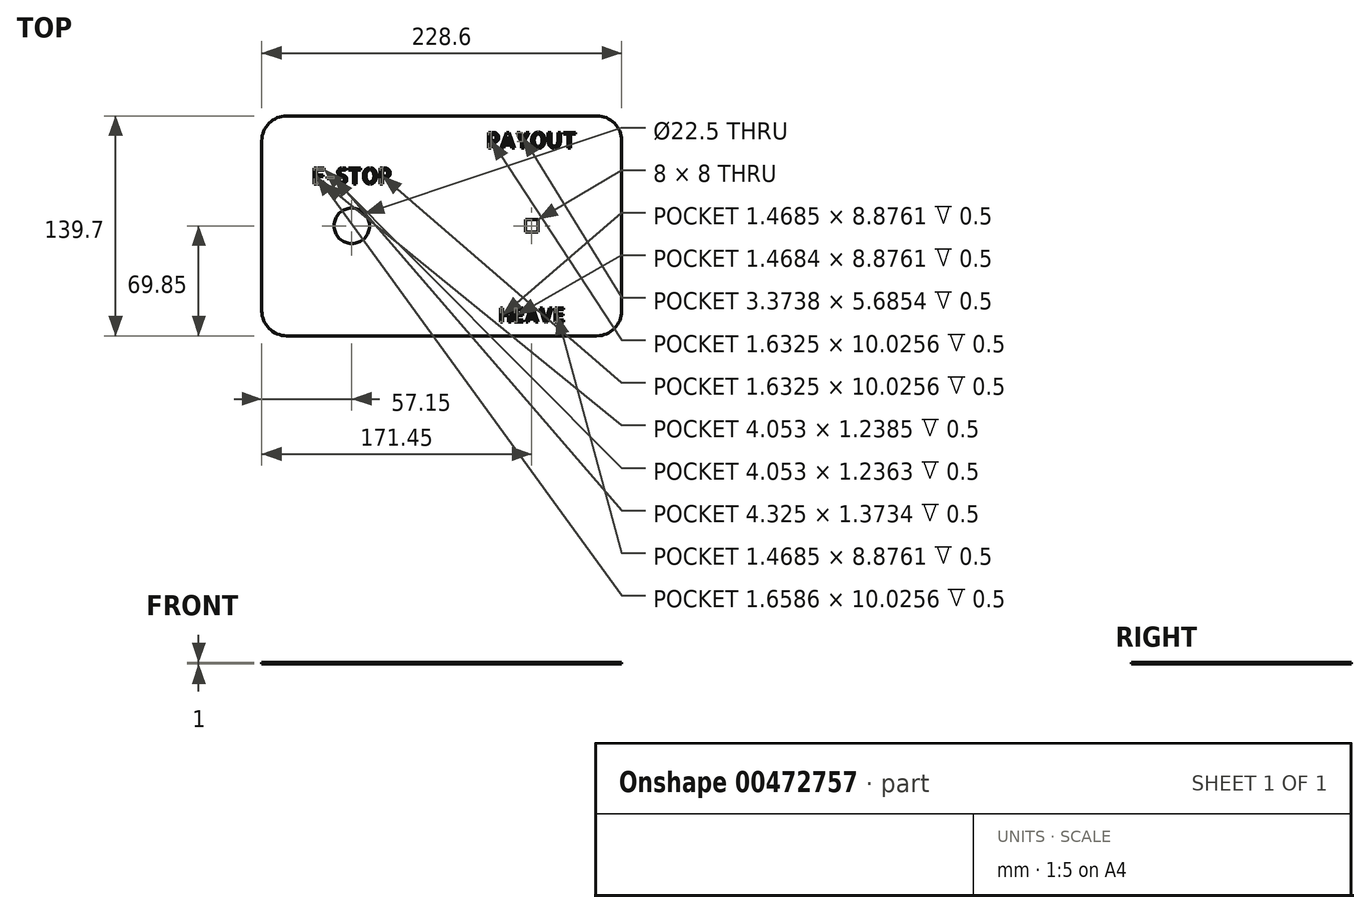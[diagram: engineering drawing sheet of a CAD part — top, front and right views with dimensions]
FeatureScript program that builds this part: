
annotation { "Feature Type Name" : "Feature", "Feature Type Description" : "" }
export const myFeature = defineFeature(function(context is Context, id is Id, definition is map)
    precondition{}
    {
        {
            var Q0;
            Q0=qCreatedBy(makeId("Top.planeOp"),FACE);
            var sketch = newSketch(context, id + "F0", { "sketchPlane" : qUnion([Q0])});
            skLineSegment(sketch, "E0.bottom", {"start": v(0, 0) * mm, "end": v(228.6, 0) * mm});
            skLineSegment(sketch, "E0.top", {"start": v(0, 139.7) * mm, "end": v(228.6, 139.7) * mm});
            skLineSegment(sketch, "E0.left", {"start": v(0, 0) * mm, "end": v(0, 139.7) * mm});
            skLineSegment(sketch, "E0.right", {"start": v(228.6, 0) * mm, "end": v(228.6, 139.7) * mm});
            skCircle(sketch, "E1", {"center": v(57.15, 69.85) * mm, "radius": 11.25 * mm});
            skLineSegment(sketch, "E2.bottom", {"start": v(167.45, 73.85) * mm, "end": v(175.45, 73.85) * mm});
            skLineSegment(sketch, "E2.top", {"start": v(167.45, 65.85) * mm, "end": v(175.45, 65.85) * mm});
            skLineSegment(sketch, "E2.left", {"start": v(167.45, 73.85) * mm, "end": v(167.45, 65.85) * mm});
            skLineSegment(sketch, "E2.right", {"start": v(175.45, 73.85) * mm, "end": v(175.45, 65.85) * mm});
            skSolve(sketch);
        }
        {
            var Q0;
            Q0 = qSketchRegion(id + "F0", true);
            extrude(context, id + "F1", {"entities" : qUnion([Q0]), "depth" : 1 * mm});
        }
        {
            var Q0;
            Q0=makeQuery(id+"F1.opExtrude","CAP_FACE",FACE,{"disambiguationData":[OSD([sQuery(id+"F0.wireOp",EDGE,"E0.bottom"),sQuery(id+"F0.wireOp",EDGE,"E0.top"),sQuery(id+"F0.wireOp",EDGE,"E0.left"),sQuery(id+"F0.wireOp",EDGE,"E0.right"),sQuery(id+"F0.wireOp",EDGE,"w9znDgtN-jEwp-FI1R-DwlJ-gQunYhQy7wCP.bottom"),sQuery(id+"F0.wireOp",EDGE,"w9znDgtN-jEwp-FI1R-DwlJ-gQunYhQy7wCP.top"),sQuery(id+"F0.wireOp",EDGE,"w9znDgtN-jEwp-FI1R-DwlJ-gQunYhQy7wCP.left"),sQuery(id+"F0.wireOp",EDGE,"w9znDgtN-jEwp-FI1R-DwlJ-gQunYhQy7wCP.right"),sQuery(id+"F0.wireOp",EDGE,"E1"),sQuery(id+"F0.wireOp",EDGE,"b33ce2e9-3de7-44f7-a6c2-fb7de444999e.sketch_text.stroke-0"),sQuery(id+"F0.wireOp",EDGE,"b33ce2e9-3de7-44f7-a6c2-fb7de444999e.sketch_text.stroke-1"),sQuery(id+"F0.wireOp",EDGE,"b33ce2e9-3de7-44f7-a6c2-fb7de444999e.sketch_text.stroke-2"),sQuery(id+"F0.wireOp",EDGE,"b33ce2e9-3de7-44f7-a6c2-fb7de444999e.sketch_text.stroke-3"),sQuery(id+"F0.wireOp",EDGE,"b33ce2e9-3de7-44f7-a6c2-fb7de444999e.sketch_text.stroke-4"),sQuery(id+"F0.wireOp",EDGE,"b33ce2e9-3de7-44f7-a6c2-fb7de444999e.sketch_text.stroke-5"),sQuery(id+"F0.wireOp",EDGE,"b33ce2e9-3de7-44f7-a6c2-fb7de444999e.sketch_text.stroke-6"),sQuery(id+"F0.wireOp",EDGE,"b33ce2e9-3de7-44f7-a6c2-fb7de444999e.sketch_text.stroke-7"),sQuery(id+"F0.wireOp",EDGE,"b33ce2e9-3de7-44f7-a6c2-fb7de444999e.sketch_text.stroke-8"),sQuery(id+"F0.wireOp",EDGE,"b33ce2e9-3de7-44f7-a6c2-fb7de444999e.sketch_text.stroke-9"),sQuery(id+"F0.wireOp",EDGE,"b33ce2e9-3de7-44f7-a6c2-fb7de444999e.sketch_text.stroke-10"),sQuery(id+"F0.wireOp",EDGE,"b33ce2e9-3de7-44f7-a6c2-fb7de444999e.sketch_text.stroke-11"),sQuery(id+"F0.wireOp",EDGE,"b33ce2e9-3de7-44f7-a6c2-fb7de444999e.sketch_text.stroke-12"),sQuery(id+"F0.wireOp",EDGE,"b33ce2e9-3de7-44f7-a6c2-fb7de444999e.sketch_text.stroke-13"),sQuery(id+"F0.wireOp",EDGE,"b33ce2e9-3de7-44f7-a6c2-fb7de444999e.sketch_text.stroke-14"),sQuery(id+"F0.wireOp",EDGE,"b33ce2e9-3de7-44f7-a6c2-fb7de444999e.sketch_text.stroke-15"),sQuery(id+"F0.wireOp",EDGE,"b33ce2e9-3de7-44f7-a6c2-fb7de444999e.sketch_text.stroke-16"),sQuery(id+"F0.wireOp",EDGE,"b33ce2e9-3de7-44f7-a6c2-fb7de444999e.sketch_text.stroke-17"),sQuery(id+"F0.wireOp",EDGE,"b33ce2e9-3de7-44f7-a6c2-fb7de444999e.sketch_text.stroke-18"),sQuery(id+"F0.wireOp",EDGE,"b33ce2e9-3de7-44f7-a6c2-fb7de444999e.sketch_text.stroke-19"),sQuery(id+"F0.wireOp",EDGE,"b33ce2e9-3de7-44f7-a6c2-fb7de444999e.sketch_text.stroke-20"),sQuery(id+"F0.wireOp",EDGE,"b33ce2e9-3de7-44f7-a6c2-fb7de444999e.sketch_text.stroke-21"),sQuery(id+"F0.wireOp",EDGE,"b33ce2e9-3de7-44f7-a6c2-fb7de444999e.sketch_text.stroke-22"),sQuery(id+"F0.wireOp",EDGE,"b33ce2e9-3de7-44f7-a6c2-fb7de444999e.sketch_text.stroke-23"),sQuery(id+"F0.wireOp",EDGE,"b33ce2e9-3de7-44f7-a6c2-fb7de444999e.sketch_text.stroke-24"),sQuery(id+"F0.wireOp",EDGE,"b33ce2e9-3de7-44f7-a6c2-fb7de444999e.sketch_text.stroke-25"),sQuery(id+"F0.wireOp",EDGE,"b33ce2e9-3de7-44f7-a6c2-fb7de444999e.sketch_text.stroke-26"),sQuery(id+"F0.wireOp",EDGE,"b33ce2e9-3de7-44f7-a6c2-fb7de444999e.sketch_text.stroke-27"),sQuery(id+"F0.wireOp",EDGE,"b33ce2e9-3de7-44f7-a6c2-fb7de444999e.sketch_text.stroke-28"),sQuery(id+"F0.wireOp",EDGE,"b33ce2e9-3de7-44f7-a6c2-fb7de444999e.sketch_text.stroke-29"),sQuery(id+"F0.wireOp",EDGE,"b33ce2e9-3de7-44f7-a6c2-fb7de444999e.sketch_text.stroke-30"),sQuery(id+"F0.wireOp",EDGE,"b33ce2e9-3de7-44f7-a6c2-fb7de444999e.sketch_text.stroke-31"),sQuery(id+"F0.wireOp",EDGE,"b33ce2e9-3de7-44f7-a6c2-fb7de444999e.sketch_text.stroke-32"),sQuery(id+"F0.wireOp",EDGE,"b33ce2e9-3de7-44f7-a6c2-fb7de444999e.sketch_text.stroke-33"),sQuery(id+"F0.wireOp",EDGE,"b33ce2e9-3de7-44f7-a6c2-fb7de444999e.sketch_text.stroke-34"),sQuery(id+"F0.wireOp",EDGE,"b33ce2e9-3de7-44f7-a6c2-fb7de444999e.sketch_text.stroke-35"),sQuery(id+"F0.wireOp",EDGE,"b33ce2e9-3de7-44f7-a6c2-fb7de444999e.sketch_text.stroke-36"),sQuery(id+"F0.wireOp",EDGE,"b33ce2e9-3de7-44f7-a6c2-fb7de444999e.sketch_text.stroke-37"),sQuery(id+"F0.wireOp",EDGE,"b33ce2e9-3de7-44f7-a6c2-fb7de444999e.sketch_text.stroke-38"),sQuery(id+"F0.wireOp",EDGE,"b33ce2e9-3de7-44f7-a6c2-fb7de444999e.sketch_text.stroke-39"),sQuery(id+"F0.wireOp",EDGE,"b33ce2e9-3de7-44f7-a6c2-fb7de444999e.sketch_text.stroke-40"),sQuery(id+"F0.wireOp",EDGE,"b33ce2e9-3de7-44f7-a6c2-fb7de444999e.sketch_text.stroke-41"),sQuery(id+"F0.wireOp",EDGE,"b33ce2e9-3de7-44f7-a6c2-fb7de444999e.sketch_text.stroke-42"),sQuery(id+"F0.wireOp",EDGE,"b33ce2e9-3de7-44f7-a6c2-fb7de444999e.sketch_text.stroke-43"),sQuery(id+"F0.wireOp",EDGE,"b33ce2e9-3de7-44f7-a6c2-fb7de444999e.sketch_text.stroke-44"),sQuery(id+"F0.wireOp",EDGE,"b33ce2e9-3de7-44f7-a6c2-fb7de444999e.sketch_text.stroke-45"),sQuery(id+"F0.wireOp",EDGE,"b33ce2e9-3de7-44f7-a6c2-fb7de444999e.sketch_text.stroke-46"),sQuery(id+"F0.wireOp",EDGE,"b33ce2e9-3de7-44f7-a6c2-fb7de444999e.sketch_text.stroke-47"),sQuery(id+"F0.wireOp",EDGE,"b33ce2e9-3de7-44f7-a6c2-fb7de444999e.sketch_text.stroke-48"),sQuery(id+"F0.wireOp",EDGE,"b33ce2e9-3de7-44f7-a6c2-fb7de444999e.sketch_text.stroke-49"),sQuery(id+"F0.wireOp",EDGE,"b33ce2e9-3de7-44f7-a6c2-fb7de444999e.sketch_text.stroke-50"),sQuery(id+"F0.wireOp",EDGE,"b33ce2e9-3de7-44f7-a6c2-fb7de444999e.sketch_text.stroke-51"),sQuery(id+"F0.wireOp",EDGE,"b33ce2e9-3de7-44f7-a6c2-fb7de444999e.sketch_text.stroke-52"),sQuery(id+"F0.wireOp",EDGE,"b33ce2e9-3de7-44f7-a6c2-fb7de444999e.sketch_text.stroke-53"),sQuery(id+"F0.wireOp",EDGE,"b33ce2e9-3de7-44f7-a6c2-fb7de444999e.sketch_text.stroke-54"),sQuery(id+"F0.wireOp",EDGE,"b33ce2e9-3de7-44f7-a6c2-fb7de444999e.sketch_text.stroke-55"),sQuery(id+"F0.wireOp",EDGE,"b33ce2e9-3de7-44f7-a6c2-fb7de444999e.sketch_text.stroke-56"),sQuery(id+"F0.wireOp",EDGE,"b33ce2e9-3de7-44f7-a6c2-fb7de444999e.sketch_text.stroke-57"),sQuery(id+"F0.wireOp",EDGE,"b33ce2e9-3de7-44f7-a6c2-fb7de444999e.sketch_text.stroke-58"),sQuery(id+"F0.wireOp",EDGE,"b33ce2e9-3de7-44f7-a6c2-fb7de444999e.sketch_text.stroke-59"),sQuery(id+"F0.wireOp",EDGE,"b33ce2e9-3de7-44f7-a6c2-fb7de444999e.sketch_text.stroke-60"),sQuery(id+"F0.wireOp",EDGE,"b33ce2e9-3de7-44f7-a6c2-fb7de444999e.sketch_text.stroke-61"),sQuery(id+"F0.wireOp",EDGE,"b33ce2e9-3de7-44f7-a6c2-fb7de444999e.sketch_text.stroke-62"),sQuery(id+"F0.wireOp",EDGE,"b33ce2e9-3de7-44f7-a6c2-fb7de444999e.sketch_text.stroke-63"),sQuery(id+"F0.wireOp",EDGE,"b33ce2e9-3de7-44f7-a6c2-fb7de444999e.sketch_text.stroke-64"),sQuery(id+"F0.wireOp",EDGE,"b33ce2e9-3de7-44f7-a6c2-fb7de444999e.sketch_text.stroke-65"),sQuery(id+"F0.wireOp",EDGE,"b33ce2e9-3de7-44f7-a6c2-fb7de444999e.sketch_text.stroke-66"),sQuery(id+"F0.wireOp",EDGE,"b33ce2e9-3de7-44f7-a6c2-fb7de444999e.sketch_text.stroke-67"),sQuery(id+"F0.wireOp",EDGE,"b33ce2e9-3de7-44f7-a6c2-fb7de444999e.sketch_text.stroke-68"),sQuery(id+"F0.wireOp",EDGE,"b33ce2e9-3de7-44f7-a6c2-fb7de444999e.sketch_text.stroke-69"),sQuery(id+"F0.wireOp",EDGE,"b33ce2e9-3de7-44f7-a6c2-fb7de444999e.sketch_text.stroke-70"),sQuery(id+"F0.wireOp",EDGE,"b33ce2e9-3de7-44f7-a6c2-fb7de444999e.sketch_text.stroke-71"),sQuery(id+"F0.wireOp",EDGE,"b33ce2e9-3de7-44f7-a6c2-fb7de444999e.sketch_text.stroke-72"),sQuery(id+"F0.wireOp",EDGE,"b33ce2e9-3de7-44f7-a6c2-fb7de444999e.sketch_text.stroke-73"),sQuery(id+"F0.wireOp",EDGE,"b33ce2e9-3de7-44f7-a6c2-fb7de444999e.sketch_text.stroke-74"),sQuery(id+"F0.wireOp",EDGE,"b33ce2e9-3de7-44f7-a6c2-fb7de444999e.sketch_text.stroke-75"),sQuery(id+"F0.wireOp",EDGE,"b33ce2e9-3de7-44f7-a6c2-fb7de444999e.sketch_text.stroke-76"),sQuery(id+"F0.wireOp",EDGE,"b33ce2e9-3de7-44f7-a6c2-fb7de444999e.sketch_text.stroke-77"),sQuery(id+"F0.wireOp",EDGE,"b33ce2e9-3de7-44f7-a6c2-fb7de444999e.sketch_text.stroke-78"),sQuery(id+"F0.wireOp",EDGE,"b33ce2e9-3de7-44f7-a6c2-fb7de444999e.sketch_text.stroke-79"),sQuery(id+"F0.wireOp",EDGE,"b33ce2e9-3de7-44f7-a6c2-fb7de444999e.sketch_text.stroke-80"),sQuery(id+"F0.wireOp",EDGE,"b33ce2e9-3de7-44f7-a6c2-fb7de444999e.sketch_text.stroke-81"),sQuery(id+"F0.wireOp",EDGE,"b33ce2e9-3de7-44f7-a6c2-fb7de444999e.sketch_text.stroke-82"),sQuery(id+"F0.wireOp",EDGE,"b33ce2e9-3de7-44f7-a6c2-fb7de444999e.sketch_text.stroke-83"),sQuery(id+"F0.wireOp",EDGE,"b33ce2e9-3de7-44f7-a6c2-fb7de444999e.sketch_text.stroke-84"),sQuery(id+"F0.wireOp",EDGE,"b33ce2e9-3de7-44f7-a6c2-fb7de444999e.sketch_text.stroke-85"),sQuery(id+"F0.wireOp",EDGE,"b33ce2e9-3de7-44f7-a6c2-fb7de444999e.sketch_text.stroke-86"),sQuery(id+"F0.wireOp",EDGE,"b33ce2e9-3de7-44f7-a6c2-fb7de444999e.sketch_text.stroke-87"),sQuery(id+"F0.wireOp",EDGE,"b33ce2e9-3de7-44f7-a6c2-fb7de444999e.sketch_text.stroke-88"),sQuery(id+"F0.wireOp",EDGE,"b33ce2e9-3de7-44f7-a6c2-fb7de444999e.sketch_text.stroke-89"),sQuery(id+"F0.wireOp",EDGE,"b33ce2e9-3de7-44f7-a6c2-fb7de444999e.sketch_text.stroke-90"),sQuery(id+"F0.wireOp",EDGE,"b33ce2e9-3de7-44f7-a6c2-fb7de444999e.sketch_text.stroke-91"),sQuery(id+"F0.wireOp",EDGE,"b33ce2e9-3de7-44f7-a6c2-fb7de444999e.sketch_text.stroke-92"),sQuery(id+"F0.wireOp",EDGE,"b33ce2e9-3de7-44f7-a6c2-fb7de444999e.sketch_text.stroke-93"),sQuery(id+"F0.wireOp",EDGE,"b33ce2e9-3de7-44f7-a6c2-fb7de444999e.sketch_text.stroke-94"),sQuery(id+"F0.wireOp",EDGE,"b33ce2e9-3de7-44f7-a6c2-fb7de444999e.sketch_text.stroke-95"),sQuery(id+"F0.wireOp",EDGE,"b33ce2e9-3de7-44f7-a6c2-fb7de444999e.sketch_text.stroke-96"),sQuery(id+"F0.wireOp",EDGE,"b33ce2e9-3de7-44f7-a6c2-fb7de444999e.sketch_text.stroke-97"),sQuery(id+"F0.wireOp",EDGE,"b33ce2e9-3de7-44f7-a6c2-fb7de444999e.sketch_text.stroke-98"),sQuery(id+"F0.wireOp",EDGE,"b33ce2e9-3de7-44f7-a6c2-fb7de444999e.sketch_text.stroke-99"),sQuery(id+"F0.wireOp",EDGE,"b33ce2e9-3de7-44f7-a6c2-fb7de444999e.sketch_text.stroke-100"),sQuery(id+"F0.wireOp",EDGE,"b33ce2e9-3de7-44f7-a6c2-fb7de444999e.sketch_text.stroke-101"),sQuery(id+"F0.wireOp",EDGE,"b33ce2e9-3de7-44f7-a6c2-fb7de444999e.sketch_text.stroke-102"),sQuery(id+"F0.wireOp",EDGE,"b33ce2e9-3de7-44f7-a6c2-fb7de444999e.sketch_text.stroke-103"),sQuery(id+"F0.wireOp",EDGE,"b33ce2e9-3de7-44f7-a6c2-fb7de444999e.sketch_text.stroke-104"),sQuery(id+"F0.wireOp",EDGE,"b33ce2e9-3de7-44f7-a6c2-fb7de444999e.sketch_text.stroke-105"),sQuery(id+"F0.wireOp",EDGE,"b33ce2e9-3de7-44f7-a6c2-fb7de444999e.sketch_text.stroke-106"),sQuery(id+"F0.wireOp",EDGE,"b33ce2e9-3de7-44f7-a6c2-fb7de444999e.sketch_text.stroke-107"),sQuery(id+"F0.wireOp",EDGE,"b33ce2e9-3de7-44f7-a6c2-fb7de444999e.sketch_text.stroke-108"),sQuery(id+"F0.wireOp",EDGE,"b33ce2e9-3de7-44f7-a6c2-fb7de444999e.sketch_text.stroke-109"),sQuery(id+"F0.wireOp",EDGE,"b33ce2e9-3de7-44f7-a6c2-fb7de444999e.sketch_text.stroke-110"),sQuery(id+"F0.wireOp",EDGE,"b33ce2e9-3de7-44f7-a6c2-fb7de444999e.sketch_text.stroke-111"),sQuery(id+"F0.wireOp",EDGE,"b33ce2e9-3de7-44f7-a6c2-fb7de444999e.sketch_text.stroke-112"),sQuery(id+"F0.wireOp",EDGE,"b33ce2e9-3de7-44f7-a6c2-fb7de444999e.sketch_text.stroke-113"),sQuery(id+"F0.wireOp",EDGE,"b33ce2e9-3de7-44f7-a6c2-fb7de444999e.sketch_text.stroke-114"),sQuery(id+"F0.wireOp",EDGE,"b33ce2e9-3de7-44f7-a6c2-fb7de444999e.sketch_text.stroke-115"),sQuery(id+"F0.wireOp",EDGE,"b33ce2e9-3de7-44f7-a6c2-fb7de444999e.sketch_text.stroke-116"),sQuery(id+"F0.wireOp",EDGE,"b33ce2e9-3de7-44f7-a6c2-fb7de444999e.sketch_text.stroke-117"),sQuery(id+"F0.wireOp",EDGE,"b33ce2e9-3de7-44f7-a6c2-fb7de444999e.sketch_text.stroke-118"),sQuery(id+"F0.wireOp",EDGE,"b33ce2e9-3de7-44f7-a6c2-fb7de444999e.sketch_text.stroke-119"),sQuery(id+"F0.wireOp",EDGE,"b33ce2e9-3de7-44f7-a6c2-fb7de444999e.sketch_text.stroke-120"),sQuery(id+"F0.wireOp",EDGE,"b33ce2e9-3de7-44f7-a6c2-fb7de444999e.sketch_text.stroke-121"),sQuery(id+"F0.wireOp",EDGE,"b33ce2e9-3de7-44f7-a6c2-fb7de444999e.sketch_text.stroke-122"),sQuery(id+"F0.wireOp",EDGE,"b33ce2e9-3de7-44f7-a6c2-fb7de444999e.sketch_text.stroke-123"),sQuery(id+"F0.wireOp",EDGE,"b33ce2e9-3de7-44f7-a6c2-fb7de444999e.sketch_text.stroke-124"),sQuery(id+"F0.wireOp",EDGE,"b33ce2e9-3de7-44f7-a6c2-fb7de444999e.sketch_text.stroke-125"),sQuery(id+"F0.wireOp",EDGE,"b33ce2e9-3de7-44f7-a6c2-fb7de444999e.sketch_text.stroke-126"),sQuery(id+"F0.wireOp",EDGE,"b33ce2e9-3de7-44f7-a6c2-fb7de444999e.sketch_text.stroke-127"),sQuery(id+"F0.wireOp",EDGE,"b33ce2e9-3de7-44f7-a6c2-fb7de444999e.sketch_text.stroke-128"),sQuery(id+"F0.wireOp",EDGE,"b33ce2e9-3de7-44f7-a6c2-fb7de444999e.sketch_text.stroke-129"),sQuery(id+"F0.wireOp",EDGE,"b33ce2e9-3de7-44f7-a6c2-fb7de444999e.sketch_text.stroke-130"),sQuery(id+"F0.wireOp",EDGE,"b33ce2e9-3de7-44f7-a6c2-fb7de444999e.sketch_text.stroke-131"),sQuery(id+"F0.wireOp",EDGE,"b33ce2e9-3de7-44f7-a6c2-fb7de444999e.sketch_text.stroke-132"),sQuery(id+"F0.wireOp",EDGE,"b33ce2e9-3de7-44f7-a6c2-fb7de444999e.sketch_text.stroke-133"),sQuery(id+"F0.wireOp",EDGE,"b33ce2e9-3de7-44f7-a6c2-fb7de444999e.sketch_text.stroke-134"),sQuery(id+"F0.wireOp",EDGE,"b33ce2e9-3de7-44f7-a6c2-fb7de444999e.sketch_text.stroke-135"),sQuery(id+"F0.wireOp",EDGE,"b33ce2e9-3de7-44f7-a6c2-fb7de444999e.sketch_text.stroke-136"),sQuery(id+"F0.wireOp",EDGE,"b33ce2e9-3de7-44f7-a6c2-fb7de444999e.sketch_text.stroke-137"),sQuery(id+"F0.wireOp",EDGE,"b33ce2e9-3de7-44f7-a6c2-fb7de444999e.sketch_text.stroke-138"),sQuery(id+"F0.wireOp",EDGE,"b33ce2e9-3de7-44f7-a6c2-fb7de444999e.sketch_text.stroke-139"),sQuery(id+"F0.wireOp",EDGE,"227bb859-5d3c-4ea1-9f34-01fb2c13be0c.sketch_text.stroke-0"),sQuery(id+"F0.wireOp",EDGE,"227bb859-5d3c-4ea1-9f34-01fb2c13be0c.sketch_text.stroke-1"),sQuery(id+"F0.wireOp",EDGE,"227bb859-5d3c-4ea1-9f34-01fb2c13be0c.sketch_text.stroke-2"),sQuery(id+"F0.wireOp",EDGE,"227bb859-5d3c-4ea1-9f34-01fb2c13be0c.sketch_text.stroke-3"),sQuery(id+"F0.wireOp",EDGE,"227bb859-5d3c-4ea1-9f34-01fb2c13be0c.sketch_text.stroke-4"),sQuery(id+"F0.wireOp",EDGE,"227bb859-5d3c-4ea1-9f34-01fb2c13be0c.sketch_text.stroke-5"),sQuery(id+"F0.wireOp",EDGE,"227bb859-5d3c-4ea1-9f34-01fb2c13be0c.sketch_text.stroke-6"),sQuery(id+"F0.wireOp",EDGE,"227bb859-5d3c-4ea1-9f34-01fb2c13be0c.sketch_text.stroke-7"),sQuery(id+"F0.wireOp",EDGE,"227bb859-5d3c-4ea1-9f34-01fb2c13be0c.sketch_text.stroke-8"),sQuery(id+"F0.wireOp",EDGE,"227bb859-5d3c-4ea1-9f34-01fb2c13be0c.sketch_text.stroke-9"),sQuery(id+"F0.wireOp",EDGE,"227bb859-5d3c-4ea1-9f34-01fb2c13be0c.sketch_text.stroke-10"),sQuery(id+"F0.wireOp",EDGE,"227bb859-5d3c-4ea1-9f34-01fb2c13be0c.sketch_text.stroke-11"),sQuery(id+"F0.wireOp",EDGE,"227bb859-5d3c-4ea1-9f34-01fb2c13be0c.sketch_text.stroke-12"),sQuery(id+"F0.wireOp",EDGE,"227bb859-5d3c-4ea1-9f34-01fb2c13be0c.sketch_text.stroke-13"),sQuery(id+"F0.wireOp",EDGE,"227bb859-5d3c-4ea1-9f34-01fb2c13be0c.sketch_text.stroke-14"),sQuery(id+"F0.wireOp",EDGE,"227bb859-5d3c-4ea1-9f34-01fb2c13be0c.sketch_text.stroke-15"),sQuery(id+"F0.wireOp",EDGE,"227bb859-5d3c-4ea1-9f34-01fb2c13be0c.sketch_text.stroke-16"),sQuery(id+"F0.wireOp",EDGE,"227bb859-5d3c-4ea1-9f34-01fb2c13be0c.sketch_text.stroke-17"),sQuery(id+"F0.wireOp",EDGE,"227bb859-5d3c-4ea1-9f34-01fb2c13be0c.sketch_text.stroke-18"),sQuery(id+"F0.wireOp",EDGE,"227bb859-5d3c-4ea1-9f34-01fb2c13be0c.sketch_text.stroke-19"),sQuery(id+"F0.wireOp",EDGE,"227bb859-5d3c-4ea1-9f34-01fb2c13be0c.sketch_text.stroke-20"),sQuery(id+"F0.wireOp",EDGE,"227bb859-5d3c-4ea1-9f34-01fb2c13be0c.sketch_text.stroke-21"),sQuery(id+"F0.wireOp",EDGE,"227bb859-5d3c-4ea1-9f34-01fb2c13be0c.sketch_text.stroke-22"),sQuery(id+"F0.wireOp",EDGE,"227bb859-5d3c-4ea1-9f34-01fb2c13be0c.sketch_text.stroke-23"),sQuery(id+"F0.wireOp",EDGE,"227bb859-5d3c-4ea1-9f34-01fb2c13be0c.sketch_text.stroke-24"),sQuery(id+"F0.wireOp",EDGE,"227bb859-5d3c-4ea1-9f34-01fb2c13be0c.sketch_text.stroke-25"),sQuery(id+"F0.wireOp",EDGE,"227bb859-5d3c-4ea1-9f34-01fb2c13be0c.sketch_text.stroke-26"),sQuery(id+"F0.wireOp",EDGE,"227bb859-5d3c-4ea1-9f34-01fb2c13be0c.sketch_text.stroke-27"),sQuery(id+"F0.wireOp",EDGE,"227bb859-5d3c-4ea1-9f34-01fb2c13be0c.sketch_text.stroke-28"),sQuery(id+"F0.wireOp",EDGE,"227bb859-5d3c-4ea1-9f34-01fb2c13be0c.sketch_text.stroke-29"),sQuery(id+"F0.wireOp",EDGE,"227bb859-5d3c-4ea1-9f34-01fb2c13be0c.sketch_text.stroke-30"),sQuery(id+"F0.wireOp",EDGE,"227bb859-5d3c-4ea1-9f34-01fb2c13be0c.sketch_text.stroke-31"),sQuery(id+"F0.wireOp",EDGE,"227bb859-5d3c-4ea1-9f34-01fb2c13be0c.sketch_text.stroke-32"),sQuery(id+"F0.wireOp",EDGE,"227bb859-5d3c-4ea1-9f34-01fb2c13be0c.sketch_text.stroke-33"),sQuery(id+"F0.wireOp",EDGE,"227bb859-5d3c-4ea1-9f34-01fb2c13be0c.sketch_text.stroke-34"),sQuery(id+"F0.wireOp",EDGE,"227bb859-5d3c-4ea1-9f34-01fb2c13be0c.sketch_text.stroke-35"),sQuery(id+"F0.wireOp",EDGE,"227bb859-5d3c-4ea1-9f34-01fb2c13be0c.sketch_text.stroke-36"),sQuery(id+"F0.wireOp",EDGE,"227bb859-5d3c-4ea1-9f34-01fb2c13be0c.sketch_text.stroke-37"),sQuery(id+"F0.wireOp",EDGE,"227bb859-5d3c-4ea1-9f34-01fb2c13be0c.sketch_text.stroke-38"),sQuery(id+"F0.wireOp",EDGE,"227bb859-5d3c-4ea1-9f34-01fb2c13be0c.sketch_text.stroke-39"),sQuery(id+"F0.wireOp",EDGE,"227bb859-5d3c-4ea1-9f34-01fb2c13be0c.sketch_text.stroke-40"),sQuery(id+"F0.wireOp",EDGE,"227bb859-5d3c-4ea1-9f34-01fb2c13be0c.sketch_text.stroke-41"),sQuery(id+"F0.wireOp",EDGE,"227bb859-5d3c-4ea1-9f34-01fb2c13be0c.sketch_text.stroke-42"),sQuery(id+"F0.wireOp",EDGE,"227bb859-5d3c-4ea1-9f34-01fb2c13be0c.sketch_text.stroke-43"),sQuery(id+"F0.wireOp",EDGE,"227bb859-5d3c-4ea1-9f34-01fb2c13be0c.sketch_text.stroke-44"),sQuery(id+"F0.wireOp",EDGE,"227bb859-5d3c-4ea1-9f34-01fb2c13be0c.sketch_text.stroke-45"),sQuery(id+"F0.wireOp",EDGE,"227bb859-5d3c-4ea1-9f34-01fb2c13be0c.sketch_text.stroke-46"),sQuery(id+"F0.wireOp",EDGE,"227bb859-5d3c-4ea1-9f34-01fb2c13be0c.sketch_text.stroke-47"),sQuery(id+"F0.wireOp",EDGE,"227bb859-5d3c-4ea1-9f34-01fb2c13be0c.sketch_text.stroke-48"),sQuery(id+"F0.wireOp",EDGE,"227bb859-5d3c-4ea1-9f34-01fb2c13be0c.sketch_text.stroke-49"),sQuery(id+"F0.wireOp",EDGE,"227bb859-5d3c-4ea1-9f34-01fb2c13be0c.sketch_text.stroke-50"),sQuery(id+"F0.wireOp",EDGE,"227bb859-5d3c-4ea1-9f34-01fb2c13be0c.sketch_text.stroke-51"),sQuery(id+"F0.wireOp",EDGE,"227bb859-5d3c-4ea1-9f34-01fb2c13be0c.sketch_text.stroke-52"),sQuery(id+"F0.wireOp",EDGE,"227bb859-5d3c-4ea1-9f34-01fb2c13be0c.sketch_text.stroke-53"),sQuery(id+"F0.wireOp",EDGE,"227bb859-5d3c-4ea1-9f34-01fb2c13be0c.sketch_text.stroke-54"),sQuery(id+"F0.wireOp",EDGE,"227bb859-5d3c-4ea1-9f34-01fb2c13be0c.sketch_text.stroke-55"),sQuery(id+"F0.wireOp",EDGE,"227bb859-5d3c-4ea1-9f34-01fb2c13be0c.sketch_text.stroke-56"),sQuery(id+"F0.wireOp",EDGE,"227bb859-5d3c-4ea1-9f34-01fb2c13be0c.sketch_text.stroke-57"),sQuery(id+"F0.wireOp",EDGE,"227bb859-5d3c-4ea1-9f34-01fb2c13be0c.sketch_text.stroke-58"),sQuery(id+"F0.wireOp",EDGE,"227bb859-5d3c-4ea1-9f34-01fb2c13be0c.sketch_text.stroke-59"),sQuery(id+"F0.wireOp",EDGE,"227bb859-5d3c-4ea1-9f34-01fb2c13be0c.sketch_text.stroke-60"),sQuery(id+"F0.wireOp",EDGE,"227bb859-5d3c-4ea1-9f34-01fb2c13be0c.sketch_text.stroke-61"),sQuery(id+"F0.wireOp",EDGE,"227bb859-5d3c-4ea1-9f34-01fb2c13be0c.sketch_text.stroke-62"),sQuery(id+"F0.wireOp",EDGE,"227bb859-5d3c-4ea1-9f34-01fb2c13be0c.sketch_text.stroke-63"),sQuery(id+"F0.wireOp",EDGE,"227bb859-5d3c-4ea1-9f34-01fb2c13be0c.sketch_text.stroke-64")])],"isStart":false});
            var sketch = newSketch(context, id + "F2", { "sketchPlane" : qUnion([Q0])});
            skText(sketch, "E3", { "text": "PAYOUT", "fontName": "AllertaStencil-Regular.ttf"});
            skText(sketch, "E4", { "text": "E-STOP", "fontName": "AllertaStencil-Regular.ttf"});
            skText(sketch, "E5", { "text": "PAYOUT", "fontName": "AllertaStencil-Regular.ttf"});
            skText(sketch, "E6", { "text": "HEAVE", "fontName": "AllertaStencil-Regular.ttf"});
            const initialGuessF2  = {"E3": [0.28093, 0.24583, 1, 0, 0.01036], "E4": [0.03186, 0.09651, 1, 0, 0.01003], "E5": [0.14285, 0.11915, 1, 0, 0.01003], "E6": [0.15034, 0.00882, 1, 0, 0.00888]};
            skSetInitialGuess(sketch, initialGuessF2);
            skSolve(sketch);
        }
        {
            var Q0;
            Q0 = qSketchRegion(id + "F2", true);
            extrude(context, id + "F3", {"entities" : qUnion([Q0]), "operationType" : NewBodyOperationType.REMOVE, "oppositeDirection" : true, "depth" : 0.5 * mm});
        }
        {
            var Q0;
            Q0=makeQuery(id+"F1.opExtrude","SWEPT_EDGE",EDGE,{"disambiguationData":[OSD([sQuery(id+"F0.wireOp",EDGE,"E0.top"),sQuery(id+"F0.wireOp",EDGE,"E0.left")])]});
            var Q1;
            Q1=makeQuery(id+"F1.opExtrude","SWEPT_EDGE",EDGE,{"disambiguationData":[OSD([sQuery(id+"F0.wireOp",EDGE,"E0.top"),sQuery(id+"F0.wireOp",EDGE,"E0.right")])]});
            var Q2;
            Q2=makeQuery(id+"F1.opExtrude","SWEPT_EDGE",EDGE,{"disambiguationData":[OSD([sQuery(id+"F0.wireOp",EDGE,"E0.bottom"),sQuery(id+"F0.wireOp",EDGE,"E0.left")])]});
            var Q3;
            Q3=makeQuery(id+"F1.opExtrude","SWEPT_EDGE",EDGE,{"disambiguationData":[OSD([sQuery(id+"F0.wireOp",EDGE,"E0.bottom"),sQuery(id+"F0.wireOp",EDGE,"E0.right")])]});
            fillet(context, id + "F4", {"entities" : qUnion([Q0, Q1, Q2, Q3]), "radius" : 15.88 * mm, "tangentPropagation" : true, "allowEdgeOverflow" : false});
        }
    });
